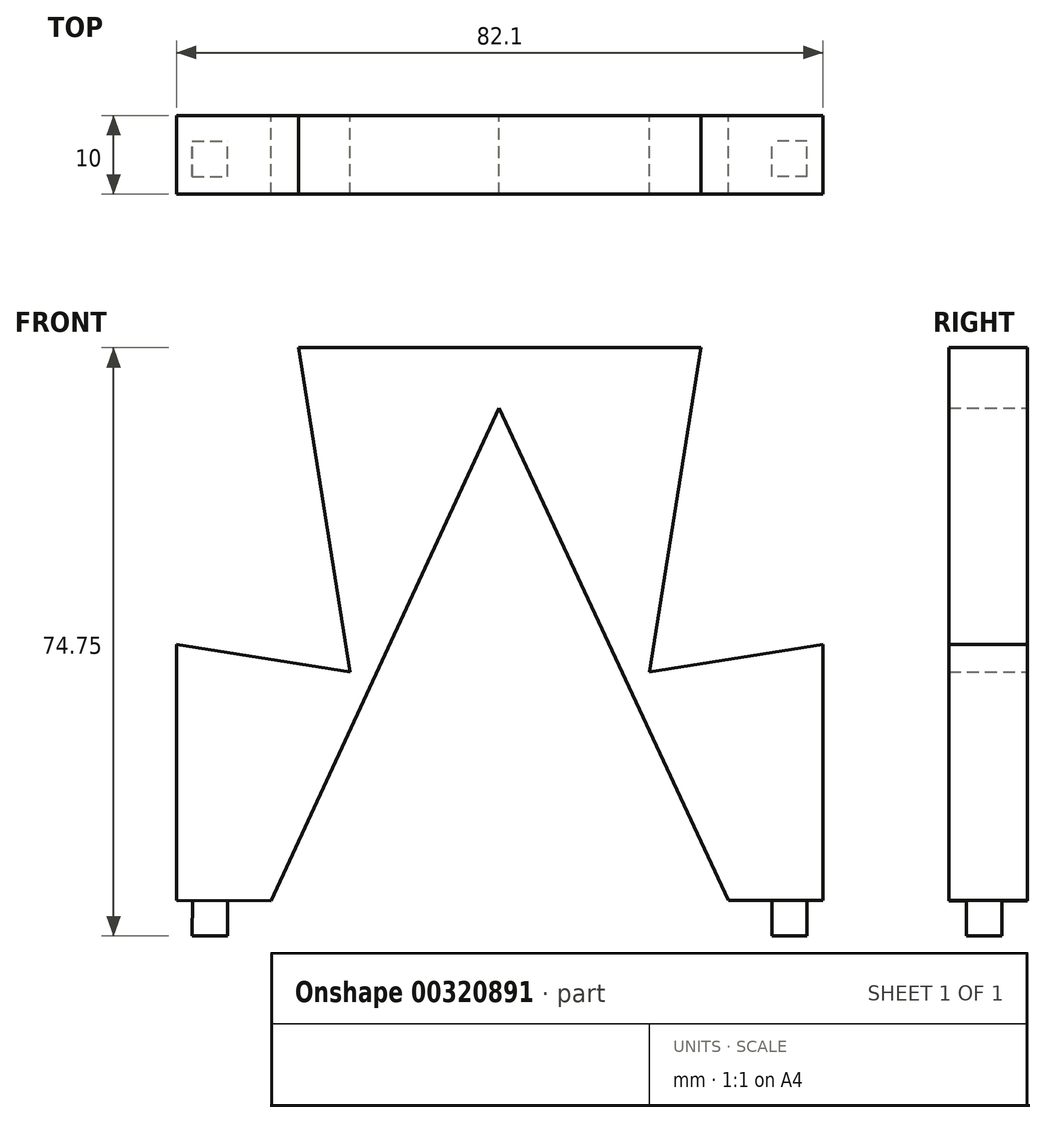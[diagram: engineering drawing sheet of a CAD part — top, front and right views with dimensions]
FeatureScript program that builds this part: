
annotation { "Feature Type Name" : "Feature", "Feature Type Description" : "" }
export const myFeature = defineFeature(function(context is Context, id is Id, definition is map)
    precondition{}
    {
        {
            var Q0;
            Q0=qCreatedBy(makeId("Front.planeOp"),FACE);
            var sketch = newSketch(context, id + "F0", { "sketchPlane" : qUnion([Q0])});
            skLineSegment(sketch, "E0", {"start": v(-25.44, 23.51) * mm, "end": v(25.66, 23.51) * mm});
            skLineSegment(sketch, "E1", {"start": v(25.66, 23.51) * mm, "end": v(19.14, -17.67) * mm});
            skLineSegment(sketch, "E2", {"start": v(19.14, -17.67) * mm, "end": v(41.16, -14.18) * mm});
            skLineSegment(sketch, "E3", {"start": v(41.16, -14.18) * mm, "end": v(41.16, -46.68) * mm});
            skLineSegment(sketch, "E4", {"start": v(-25.44, 23.51) * mm, "end": v(-18.92, -17.67) * mm});
            skLineSegment(sketch, "E5", {"start": v(-18.92, -17.67) * mm, "end": v(-40.94, -14.18) * mm});
            skLineSegment(sketch, "E6", {"start": v(-40.94, -14.18) * mm, "end": v(-40.94, -46.68) * mm});
            skLineSegment(sketch, "E7", {"start": v(41.16, -46.68) * mm, "end": v(29.16, -46.68) * mm});
            skLineSegment(sketch, "E8", {"start": v(29.16, -46.68) * mm, "end": v(0, 15.85) * mm});
            skLineSegment(sketch, "E9", {"start": v(0, 15.85) * mm, "end": v(-28.94, -46.78) * mm});
            skLineSegment(sketch, "E10", {"start": v(-28.94, -46.78) * mm, "end": v(-40.94, -46.68) * mm});
            skSolve(sketch);
        }
        {
            var Q0;
            Q0=makeQuery(id+"F0.imprint","IMPRINT",FACE,{"disambiguationData":[TD([[makeQuery(id+"F0.imprint","IMPRINT",EDGE,{"derivedFrom":sQuery(id+"F0.wireOp",EDGE,"E0")}),-1.0]])]});
            extrude(context, id + "F1", {"entities" : qUnion([Q0]), "depth" : 10 * mm});
        }
        {
            var Q0;
            Q0=makeQuery(id+"F1.opExtrude","SWEPT_FACE",FACE,{"disambiguationData":[OSD([sQuery(id+"F0.wireOp",EDGE,"E10")])]});
            var sketch = newSketch(context, id + "F2", { "sketchPlane" : qUnion([Q0])});
            skLineSegment(sketch, "E11", {"start": v(-40.55, 10) * mm, "end": v(-38.54, 7.77) * mm});
            skLineSegment(sketch, "E12.bottom", {"start": v(-38.54, 7.77) * mm, "end": v(-34.04, 7.77) * mm});
            skLineSegment(sketch, "E12.top", {"start": v(-38.54, 3.27) * mm, "end": v(-34.04, 3.27) * mm});
            skLineSegment(sketch, "E12.left", {"start": v(-38.54, 7.77) * mm, "end": v(-38.54, 3.27) * mm});
            skLineSegment(sketch, "E12.right", {"start": v(-34.04, 7.77) * mm, "end": v(-34.04, 3.27) * mm});
            skSolve(sketch);
        }
        {
            var Q0;
            Q0 = qSketchRegion(id + "F2", true);
            extrude(context, id + "F3", {"entities" : qUnion([Q0]), "operationType" : NewBodyOperationType.ADD, "depth" : 4.5 * mm});
        }
        {
            var Q0;
            Q0=makeQuery(id+"F1.opExtrude","SWEPT_FACE",FACE,{"disambiguationData":[OSD([sQuery(id+"F0.wireOp",EDGE,"E7")])]});
            var sketch = newSketch(context, id + "F4", { "sketchPlane" : qUnion([Q0])});
            skLineSegment(sketch, "E13", {"start": v(41.16, 10) * mm, "end": v(39.15, 7.77) * mm});
            skLineSegment(sketch, "E14.bottom", {"start": v(39.15, 7.77) * mm, "end": v(34.65, 7.77) * mm});
            skLineSegment(sketch, "E14.top", {"start": v(39.15, 3.27) * mm, "end": v(34.65, 3.27) * mm});
            skLineSegment(sketch, "E14.left", {"start": v(39.15, 7.77) * mm, "end": v(39.15, 3.27) * mm});
            skLineSegment(sketch, "E14.right", {"start": v(34.65, 7.77) * mm, "end": v(34.65, 3.27) * mm});
            skSolve(sketch);
        }
        {
            var Q0;
            Q0 = qSketchRegion(id + "F4", true);
            extrude(context, id + "F5", {"entities" : qUnion([Q0]), "operationType" : NewBodyOperationType.ADD, "depth" : 4.5 * mm});
        }
    });
